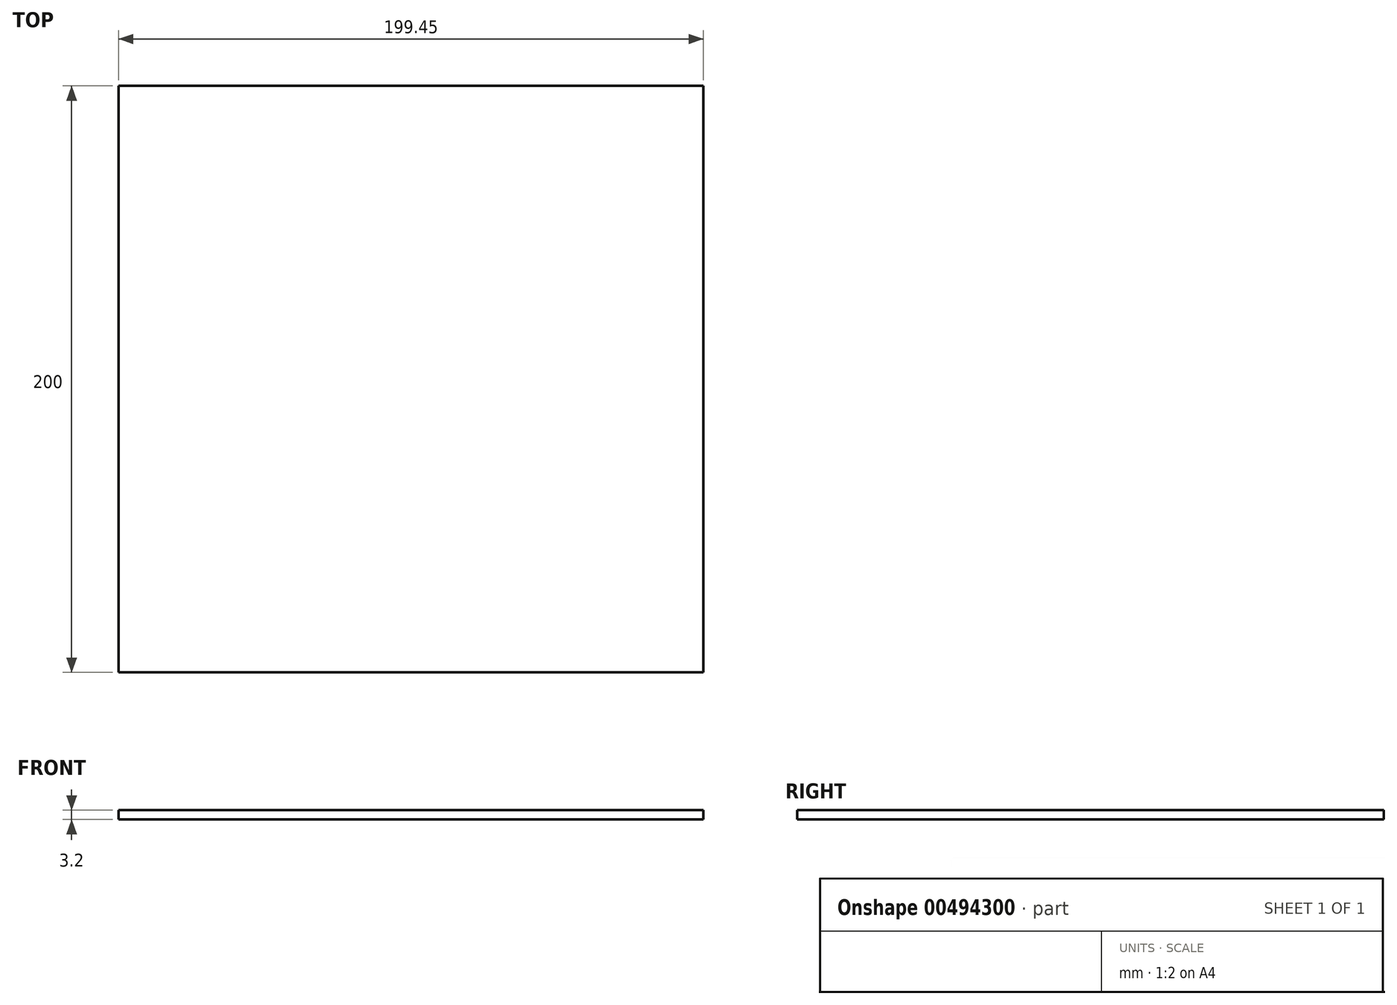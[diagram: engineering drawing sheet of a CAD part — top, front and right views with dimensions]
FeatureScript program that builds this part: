
annotation { "Feature Type Name" : "Feature", "Feature Type Description" : "" }
export const myFeature = defineFeature(function(context is Context, id is Id, definition is map)
    precondition{}
    {
        {
            var Q0;
            Q0=qCreatedBy(makeId("Top.planeOp"),FACE);
            var sketch = newSketch(context, id + "F0", { "sketchPlane" : qUnion([Q0])});
            skLineSegment(sketch, "E0.bottom", {"start": v(-99.83, 99.69) * mm, "end": v(99.62, 99.69) * mm});
            skLineSegment(sketch, "E0.top", {"start": v(-99.83, -100.31) * mm, "end": v(99.62, -100.31) * mm});
            skLineSegment(sketch, "E0.left", {"start": v(-99.83, 99.69) * mm, "end": v(-99.83, -100.31) * mm});
            skLineSegment(sketch, "E0.right", {"start": v(99.62, 99.69) * mm, "end": v(99.62, -100.31) * mm});
            skSolve(sketch);
        }
        {
            var Q0;
            Q0 = qSketchRegion(id + "F0", true);
            extrude(context, id + "F1", {"entities" : qUnion([Q0]), "depth" : 3.2 * mm});
        }
        {
            var Q0;
            Q0=makeQuery(id+"F1.opExtrude","CAP_FACE",FACE,{"disambiguationData":[OSD([sQuery(id+"F0.wireOp",EDGE,"E0.bottom"),sQuery(id+"F0.wireOp",EDGE,"E0.top"),sQuery(id+"F0.wireOp",EDGE,"E0.left"),sQuery(id+"F0.wireOp",EDGE,"E0.right")])],"isStart":false});
            var sketch = newSketch(context, id + "F2", { "sketchPlane" : qUnion([Q0])});
            skSolve(sketch);
        }
        {
            var Q0;
            Q0=makeQuery(id+"F2.imprint","IMPRINT",FACE,{"disambiguationData":[TD([[makeQuery(id+"F2.imprint","IMPRINT",EDGE,{"derivedFrom":makeQuery(id+"F1.opExtrude","CAP_EDGE",EDGE,{"disambiguationData":[OSD([sQuery(id+"F0.wireOp",EDGE,"E0.bottom")])],"isStart":false})}),-1.0]])]});
            var sketch = newSketch(context, id + "F3", { "sketchPlane" : qUnion([Q0])});
            skCircle(sketch, "E1", {"center": v(38.41, -38.9) * mm, "radius": 31.47 * mm});
            skSolve(sketch);
        }
        {
            var Q0;
            Q0=sQuery(id+"F3.wireOp",EDGE,"E1");
            extrude(context, id + "F4", {"bodyType" : ToolBodyType.SURFACE, "surfaceEntities" : qUnion([Q0]), "depth" : 13.9 * mm, "offsetDistance" : 25 * mm});
        }
    });
